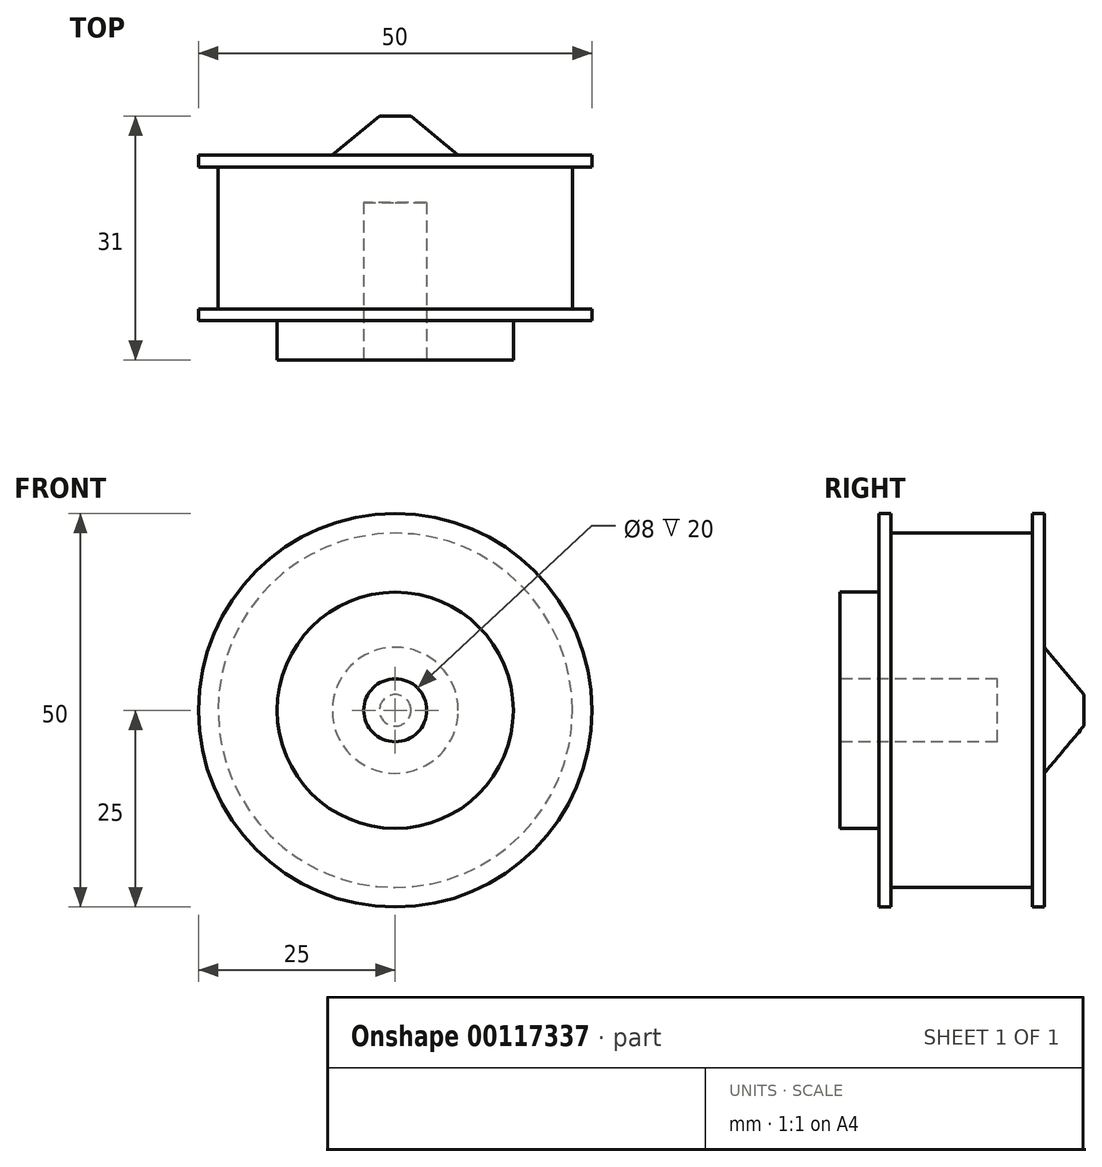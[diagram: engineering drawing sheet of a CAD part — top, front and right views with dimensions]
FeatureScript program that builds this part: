
annotation { "Feature Type Name" : "Feature", "Feature Type Description" : "" }
export const myFeature = defineFeature(function(context is Context, id is Id, definition is map)
    precondition{}
    {
        {
            var Q0;
            Q0=qCreatedBy(makeId("Front.planeOp"),FACE);
            var sketch = newSketch(context, id + "F0", { "sketchPlane" : qUnion([Q0])});
            skCircle(sketch, "E0", {"center": v(0, 0) * mm, "radius": 25 * mm});
            skSolve(sketch);
        }
        {
            var Q0;
            Q0 = qSketchRegion(id + "F0", true);
            extrude(context, id + "F1", {"entities" : qUnion([Q0]), "depth" : 1.5 * mm});
        }
        {
            var Q0;
            Q0=makeQuery(id+"F1.opExtrude","CAP_FACE",FACE,{"disambiguationData":[OSD([sQuery(id+"F0.wireOp",EDGE,"E0")])],"isStart":false});
            var sketch = newSketch(context, id + "F2", { "sketchPlane" : qUnion([Q0])});
            skCircle(sketch, "E1", {"center": v(0, 0) * mm, "radius": 22.5 * mm});
            skSolve(sketch);
        }
        {
            var Q0;
            Q0 = qSketchRegion(id + "F2", true);
            extrude(context, id + "F3", {"entities" : qUnion([Q0]), "operationType" : NewBodyOperationType.ADD, "depth" : 18 * mm});
        }
        {
            var Q0;
            Q0=makeQuery(id+"F3.opExtrude","CAP_FACE",FACE,{"disambiguationData":[OSD([sQuery(id+"F2.wireOp",EDGE,"E1")])],"isStart":false});
            var sketch = newSketch(context, id + "F4", { "sketchPlane" : qUnion([Q0])});
            skCircle(sketch, "E2", {"center": v(0, 0) * mm, "radius": 25 * mm});
            skSolve(sketch);
        }
        {
            var Q0;
            Q0 = qSketchRegion(id + "F4", true);
            extrude(context, id + "F5", {"entities" : qUnion([Q0]), "operationType" : NewBodyOperationType.ADD, "depth" : 1.5 * mm});
        }
        {
            var Q0;
            Q0=makeQuery(id+"F5.opExtrude","CAP_FACE",FACE,{"disambiguationData":[OSD([sQuery(id+"F4.wireOp",EDGE,"E2")])],"isStart":false});
            var sketch = newSketch(context, id + "F6", { "sketchPlane" : qUnion([Q0])});
            skCircle(sketch, "E3", {"center": v(0, 0) * mm, "radius": 15 * mm});
            skSolve(sketch);
        }
        {
            var Q0;
            Q0 = qSketchRegion(id + "F6", true);
            extrude(context, id + "F7", {"entities" : qUnion([Q0]), "operationType" : NewBodyOperationType.ADD, "depth" : 5 * mm});
        }
        {
            var Q0;
            Q0=qCreatedBy(makeId("Right.planeOp"),FACE);
            var sketch = newSketch(context, id + "F8", { "sketchPlane" : qUnion([Q0])});
            skLineSegment(sketch, "E4", {"start": v(0, 0) * mm, "end": v(5, 0) * mm});
            skLineSegment(sketch, "E5", {"start": v(5, 0) * mm, "end": v(5, -2) * mm});
            skLineSegment(sketch, "E6", {"start": v(5, -2) * mm, "end": v(0, -8) * mm});
            skLineSegment(sketch, "E7", {"start": v(0, -8) * mm, "end": v(0, 0) * mm});
            skLineSegment(sketch, "E8", {"start": v(0, 0) * mm, "end": v(20.4, 0) * mm});
            skSolve(sketch);
        }
        {
            var Q0;
            {var subQ0=sQuery(id+"F8.wireOp",EDGE,"E5");Q0=makeQuery(id+"F8.imprint","IMPRINT",FACE,{"disambiguationData":[TD([[makeQuery(id+"F8.imprint","IMPRINT",EDGE,{"derivedFrom":subQ0}),-1.0]])]});}
            var Q1;
            Q1=sQuery(id+"F8.wireOp",EDGE,"E8");
            revolve(context, id + "F9", {"operationType" : NewBodyOperationType.ADD, "entities" : qUnion([Q0]), "axis" : qUnion([Q1]), "revolveType" : RevolveType.FULL});
        }
        {
            var Q0;
            Q0=makeQuery(id+"F7.opExtrude","CAP_FACE",FACE,{"disambiguationData":[OSD([sQuery(id+"F6.wireOp",EDGE,"E3")])],"isStart":false});
            var sketch = newSketch(context, id + "F10", { "sketchPlane" : qUnion([Q0])});
            skCircle(sketch, "E9", {"center": v(0, 0) * mm, "radius": 4 * mm});
            skSolve(sketch);
        }
        {
            var Q0;
            Q0 = qSketchRegion(id + "F10", true);
            extrude(context, id + "F11", {"entities" : qUnion([Q0]), "operationType" : NewBodyOperationType.REMOVE, "oppositeDirection" : true, "depth" : 20 * mm});
        }
    });
